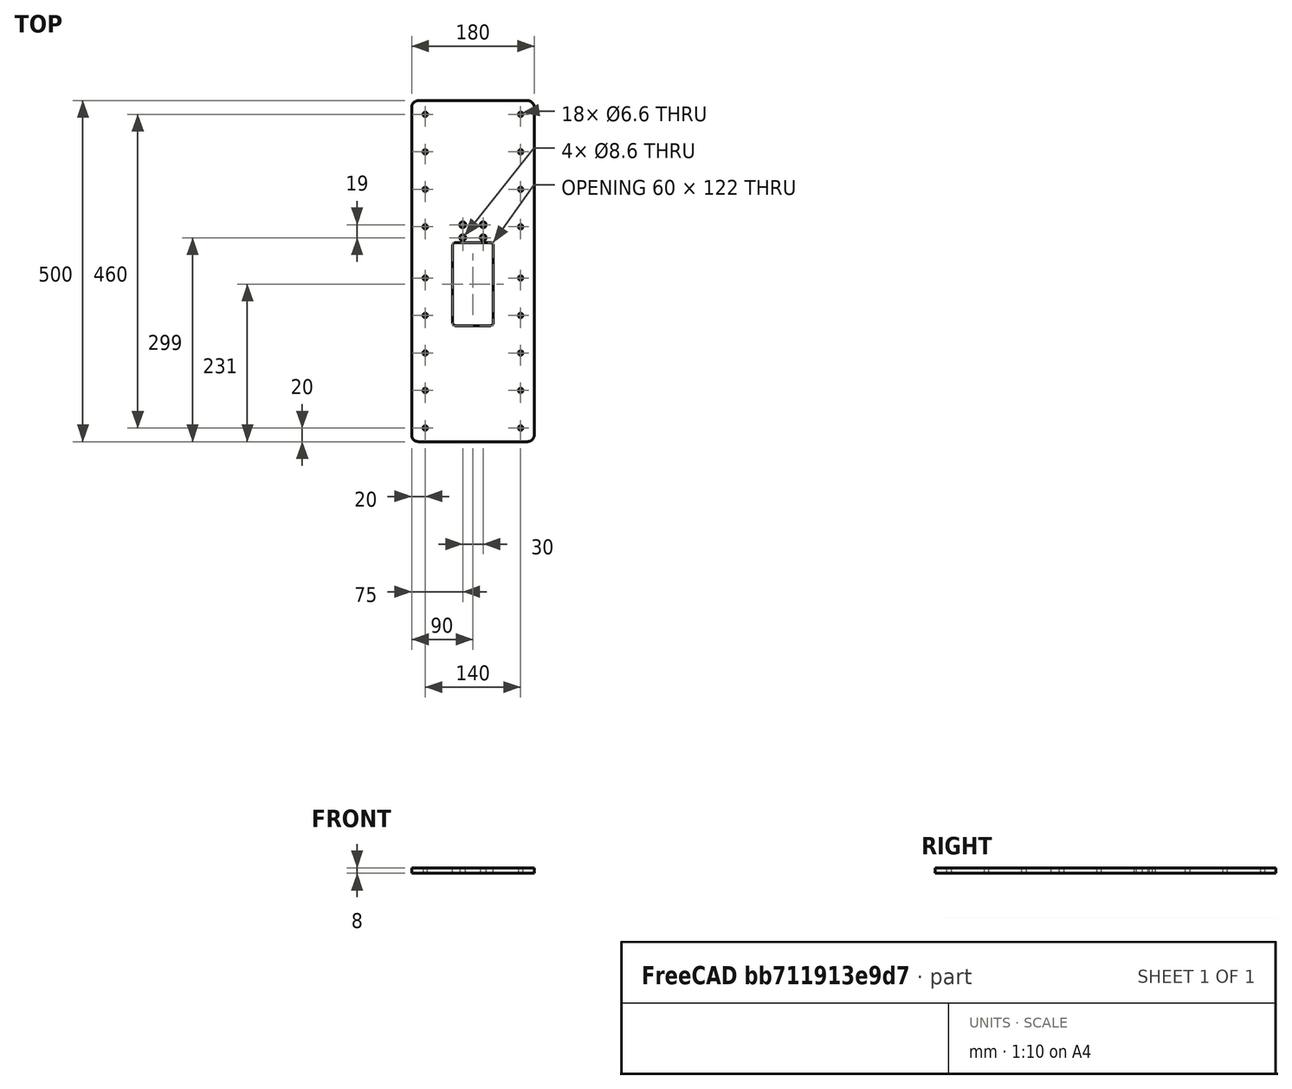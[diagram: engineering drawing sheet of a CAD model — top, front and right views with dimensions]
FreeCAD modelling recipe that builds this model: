
FCSTD DOCUMENT  (FreeCAD 0.17R12848 (Git))
Label: bienenwaage-oben
License: All rights reserved
LicenseURL: http://en.wikipedia.org/wiki/All_rights_reserved
objects: Sketcher::SketchObject×1, PartDesign::Pad×1, PartDesign::Body×1
note: 4 computed .brp shape members not serialized (recipe doc carries the construction recipe); baked Part::Feature solids carry a one-line shape summary decoded from their .brp

FEATURE [Sketcher::SketchObject] Sketch
  MapMode = 5
  Support = -> [XY_Plane]
  sketch-geometry (50):
    g0: Circle CenterX=75 CenterY=318 CenterZ=0 NormalX=0 NormalY=0 NormalZ=1 AngleXU=0 Radius=4.3
    g1: Circle CenterX=105 CenterY=318 CenterZ=0 NormalX=0 NormalY=0 NormalZ=1 AngleXU=0 Radius=4.3
    g2: Circle CenterX=105 CenterY=299 CenterZ=0 NormalX=0 NormalY=0 NormalZ=1 AngleXU=0 Radius=4.3
    g3: Circle CenterX=75 CenterY=299 CenterZ=0 NormalX=0 NormalY=0 NormalZ=1 AngleXU=0 Radius=4.3
    g4: LineSegment StartX=65 StartY=170 StartZ=0 EndX=115 EndY=170 EndZ=0
    g5: LineSegment StartX=60 StartY=175 StartZ=0 EndX=60 EndY=287 EndZ=0
    g6: LineSegment StartX=65 StartY=292 StartZ=0 EndX=115 EndY=292 EndZ=0
    g7: LineSegment StartX=120 StartY=287 StartZ=0 EndX=120 EndY=175 EndZ=0
    g8: LineSegment StartX=180 StartY=10 StartZ=0 EndX=180 EndY=490 EndZ=0
    g9: LineSegment StartX=0 StartY=490 StartZ=0 EndX=0 EndY=10 EndZ=0
    g10: GeomPoint X=0 Y=500 Z=0
    g11: GeomPoint X=180 Y=500 Z=0
    g12: LineSegment StartX=10 StartY=500 StartZ=0 EndX=170 EndY=500 EndZ=0
    g13: LineSegment StartX=10 StartY=0 StartZ=0 EndX=170 EndY=0 EndZ=0
    g14: Circle CenterX=20 CenterY=20 CenterZ=0 NormalX=0 NormalY=0 NormalZ=1 AngleXU=0 Radius=3.3
    g15: Circle CenterX=20 CenterY=75 CenterZ=0 NormalX=0 NormalY=0 NormalZ=1 AngleXU=0 Radius=3.3
    g16: Circle CenterX=20 CenterY=130 CenterZ=0 NormalX=0 NormalY=0 NormalZ=1 AngleXU=0 Radius=3.3
    g17: Circle CenterX=20 CenterY=185 CenterZ=0 NormalX=0 NormalY=0 NormalZ=1 AngleXU=0 Radius=3.3
    g18: Circle CenterX=20 CenterY=480 CenterZ=0 NormalX=0 NormalY=0 NormalZ=1 AngleXU=0 Radius=3.3
    g19: Circle CenterX=20 CenterY=425 CenterZ=0 NormalX=0 NormalY=0 NormalZ=1 AngleXU=0 Radius=3.3
    g20: Circle CenterX=20 CenterY=370 CenterZ=0 NormalX=0 NormalY=0 NormalZ=1 AngleXU=0 Radius=3.3
    g21: Circle CenterX=20 CenterY=315 CenterZ=0 NormalX=0 NormalY=0 NormalZ=1 AngleXU=0 Radius=3.3
    g22: Circle CenterX=20 CenterY=240 CenterZ=0 NormalX=0 NormalY=0 NormalZ=1 AngleXU=0 Radius=3.3
    g23: Circle CenterX=160 CenterY=480 CenterZ=0 NormalX=0 NormalY=0 NormalZ=1 AngleXU=0 Radius=3.3
    g24: Circle CenterX=160 CenterY=425 CenterZ=0 NormalX=0 NormalY=0 NormalZ=1 AngleXU=0 Radius=3.3
    g25: Circle CenterX=160 CenterY=370 CenterZ=0 NormalX=0 NormalY=0 NormalZ=1 AngleXU=0 Radius=3.3
    g26: Circle CenterX=160 CenterY=315 CenterZ=0 NormalX=0 NormalY=0 NormalZ=1 AngleXU=0 Radius=3.3
    g27: Circle CenterX=160 CenterY=240 CenterZ=0 NormalX=0 NormalY=0 NormalZ=1 AngleXU=0 Radius=3.3
    g28: Circle CenterX=160 CenterY=20 CenterZ=0 NormalX=0 NormalY=0 NormalZ=1 AngleXU=0 Radius=3.3
    g29: Circle CenterX=160 CenterY=75 CenterZ=0 NormalX=0 NormalY=0 NormalZ=1 AngleXU=0 Radius=3.3
    g30: Circle CenterX=160 CenterY=130 CenterZ=0 NormalX=0 NormalY=0 NormalZ=1 AngleXU=0 Radius=3.3
    g31: Circle CenterX=160 CenterY=185 CenterZ=0 NormalX=0 NormalY=0 NormalZ=1 AngleXU=0 Radius=3.3
    g32: GeomPoint X=0 Y=500 Z=0
    g33: ArcOfCircle CenterX=10 CenterY=490 CenterZ=0 NormalX=0 NormalY=0 NormalZ=1 AngleXU=0 Radius=10 StartAngle=1.5708 EndAngle=3.14159
    g34: GeomPoint X=180 Y=500 Z=0
    g35: ArcOfCircle CenterX=170 CenterY=490 CenterZ=0 NormalX=0 NormalY=0 NormalZ=1 AngleXU=0 Radius=10 StartAngle=0 EndAngle=1.5708
    g36: GeomPoint X=180 Y=0 Z=0
    g37: ArcOfCircle CenterX=170 CenterY=10 CenterZ=0 NormalX=0 NormalY=0 NormalZ=1 AngleXU=0 Radius=10 StartAngle=4.71239 EndAngle=6.28319
    g38: ArcOfCircle CenterX=10 CenterY=10 CenterZ=0 NormalX=0 NormalY=0 NormalZ=1 AngleXU=0 Radius=10 StartAngle=3.14159 EndAngle=4.71239
    g39: GeomPoint X=60 Y=292 Z=0
    g40: GeomPoint X=120 Y=292 Z=0
    g41: GeomPoint X=60 Y=170 Z=0
    g42: ArcOfCircle CenterX=115 CenterY=175 CenterZ=0 NormalX=0 NormalY=0 NormalZ=1 AngleXU=0 Radius=5 StartAngle=4.71239 EndAngle=6.28319
    g43: GeomPoint X=120 Y=170 Z=0
    g44: GeomPoint X=60 Y=170 Z=0
    g45: ArcOfCircle CenterX=65 CenterY=175 CenterZ=0 NormalX=0 NormalY=0 NormalZ=1 AngleXU=0 Radius=5 StartAngle=3.14159 EndAngle=4.71239
    g46: GeomPoint X=60 Y=292 Z=0
    g47: ArcOfCircle CenterX=65 CenterY=287 CenterZ=0 NormalX=0 NormalY=0 NormalZ=1 AngleXU=0 Radius=5 StartAngle=1.5708 EndAngle=3.14159
    g48: GeomPoint X=120 Y=292 Z=0
    g49: ArcOfCircle CenterX=115 CenterY=287 CenterZ=0 NormalX=0 NormalY=0 NormalZ=1 AngleXU=0 Radius=5 StartAngle=0 EndAngle=1.5708
  constraints (125):
    c: DistanceY(g39,g3) = 7
    c: DistanceX(g39,g3) = 15
    c: DistanceX(g3,g2) = 30
    c: DistanceY(g2,g1) = 19
    c: Radius(g0) = 4.3
    c: Radius(g3) = 4.3
    c: Radius(g2) = 4.3
    c: Radius(g1) = 4.3
    c: Horizontal(g4)
    c: DistanceX(g-1,g10) = 0
    c: DistanceX(g0,g3) = 0
    c: DistanceX(g1,g2) = 0
    c: DistanceY(g0,g1) = 0
    c: DistanceY(g-1,g10) = 500
    c: DistanceX(g39,g40) = 60
    c: DistanceY(g-1,g39) = 292
    c: DistanceY(g3,g2) = 0
    c: Horizontal(g6)
    c: DistanceX(g10,g11) = 180
    c: DistanceY(g11,g10) = 0
    c: Horizontal(g12,g12)
    c: Vertical(g5)
    c: Vertical(g7)
    c: Vertical(g8)
    c: Vertical(g9)
    c: DistanceX(g-1,g41) = 60
    c: DistanceY(g-1,g41) = 170
    c: Horizontal(g9,g8)
    c: Vertical(g28,g29)
    c: Vertical(g29,g30)
    c: Vertical(g30,g31)
    c: Vertical(g31,g27)
    c: Vertical(g27,g26)
    c: Vertical(g26,g25)
    c: Vertical(g25,g24)
    c: Vertical(g24,g23)
    c: Vertical(g18,g19)
    c: Vertical(g19,g20)
    c: Vertical(g20,g21)
    c: Vertical(g21,g22)
    c: Vertical(g22,g17)
    c: Vertical(g17,g16)
    c: Vertical(g16,g15)
    c: Vertical(g15,g14)
    c: Horizontal(g14,g28)
    c: Horizontal(g15,g29)
    c: Horizontal(g16,g30)
    c: Horizontal(g17,g31)
    c: Horizontal(g27,g22)
    c: Horizontal(g26,g21)
    c: Horizontal(g25,g20)
    c: Horizontal(g19,g24)
    c: Horizontal(g23,g18)
    c: Radius(g18) = 3.3
    c: Equal(g18,g23)
    c: Equal(g18,g24)
    c: Equal(g18,g19)
    c: Equal(g18,g25)
    c: Equal(g18,g20)
    c: Equal(g18,g21)
    c: Equal(g18,g26)
    c: Equal(g18,g27)
    c: Equal(g18,g22)
    c: Equal(g18,g17)
    c: Equal(g18,g31)
    c: Equal(g18,g30)
    c: Equal(g18,g16)
    c: Equal(g18,g15)
    c: Equal(g18,g29)
    c: Equal(g18,g28)
    c: Equal(g18,g14)
    c: DistanceX(g-1,g14) = 20
    c: DistanceX(g28,g36) = 20
    c: DistanceY(g-1,g14) = 20
    c: DistanceY(g14,g15) = 55
    c: DistanceY(g15,g16) = 55
    c: DistanceY(g16,g17) = 55
    c: DistanceY(g23,g11) = 20
    c: DistanceY(g19,g23) = 55
    c: DistanceY(g25,g19) = 55
    c: DistanceY(g26,g25) = 55
    c: DistanceY(g17,g27) = 55
    c: Coincident(g32,g10)
    c: Tangent(g9,g33) = -1.5708
    c: Tangent(g12,g33) = 1.5708
    c: Distance(g10,g12) = 10
    c: Distance(g10,g9) = 10
    c: Coincident(g34,g11)
    c: Tangent(g12,g35) = 1.5708
    c: Tangent(g8,g35) = -1.5708
    c: Distance(g11,g8) = 10
    c: Distance(g12,g11) = 10
    c: DistanceY(g12,g10) = 0
    c: Tangent(g8,g37) = -1.5708
    c: Tangent(g13,g37) = -1.5708
    c: Distance(g36,g8) = 10
    c: Tangent(g9,g38) = -1.5708
    c: Tangent(g13,g38) = -1.5708
    c: Distance(g9,g-1) = 10
    c: Distance(g13,g-1) = 10
    c: DistanceY(g13,g-1) = 0
    c: Distance(g13,g36) = 10
    c: Tangent(g7,g42) = 1.5708
    c: Tangent(g4,g42) = -1.5708
    c: DistanceX(g41,g43) = 60
    c: DistanceY(g43,g41) = 0
    c: Distance(g43,g7) = 5
    c: Coincident(g44,g41)
    c: Tangent(g5,g45) = 1.5708
    c: Tangent(g4,g45) = -1.5708
    c: Distance(g41,g5) = 5
    c: Distance(g41,g4) = 5
    c: DistanceY(g4,g41) = 0
    c: Tangent(g6,g47) = 1.5708
    c: Tangent(g5,g47) = 1.5708
    c: Distance(g46,g6) = 5
    c: Distance(g46,g5) = 5
    c: Coincident(g46,g39)
    c: DistanceY(g39,g6) = 0
    c: Coincident(g48,g40)
    c: Tangent(g7,g49) = 1.5708
    c: Tangent(g6,g49) = 1.5708
    c: Distance(g40,g6) = 5
    c: Distance(g40,g7) = 5
    c: DistanceY(g40,g39) = 0
FEATURE [PartDesign::Pad] Pad
  Length = 8
  Length2 = 100
  Profile = -> Sketch
  Type = 0
FEATURE [PartDesign::Body] Body
  Group = -> [Sketch,Pad]
  Origin = -> Origin
  Tip = -> Pad
